# Revit family: KingswayGroup_Mrrrs_Anti-LigatureMirror
name_source: partatom
category: Specialty Equipment
units: mm (PartAtom-declared; Revit-internal decimal feet)

## family parameters
Always vertical = Yes
Cut with Voids When Loaded = No
Part Type = Normal
Room Calculation Point = No
Round Connector Dimension = Use Diameter
Shared = No
Work Plane-Based = No

## types (1)
- KingswayGroup_Mrrrs_Anti-LigatureMirror
    AssetType = Fixed
    BIMObjectName = KingswayGroup_Mirrors_Anti-LigatureMirror
    Category = Pr_40_30_53:Mirrors
    Color = For full range of available finishes and colours, contact Kingsway Group
    Default Elevation = 0 mm  [stored 0 ft]
    Description = Anti-Ligature Mirror
    DurationUnit = year
    Features = Shatter-resistant for improved safety, the KG231 Anti-Ligature Mirror is manufactured from high-strength materials to ensure durable performance. It features an impact-resistant and shatter-resistant polycarbonate mirror piece housed within an anti-ligature aluminium frame.
    Finish = For full range of available finishes and colours, contact Kingsway Group
    Manufacturer = Kingsway Group
    ManufacturerName = Kingsway Group
    ManufacturerURL = https://kingswaygroupglobal.com
    Material = Aluminium, Glass
    MirrorMaterial = NBS_Concept
    Model = KG231
    ModelNumber = KG231
    ModelReference = Anti-Ligature Mirror
    Name = Mirrors_Anti-LigatureMirror_KG231_KingswayGroup
    NominalHeight = 915 mm  [stored 3.00197 ft]
    NominalLength = 460 mm  [stored 1.50919 ft]
    NominalWidth = 13 mm
    PlateMaterial = NBS_Concept
    ProductInformation = https://kingswaygroupglobal.com
    Size = 460 x 915 x 13 mm
    URL = https://kingswaygroupglobal.com
    Uniclass2015Code = Pr_40_30_53
    Uniclass2015Title = Mirrors
    Uniclass2015Version = Products v1.36
    Version = 1
    WarrantyDescription = 5-Year Guarantee *For faulty manufacture and not for damage
    WarrantyDurationParts = 5
    WarrantyDurationUnit = year

note: [stored X ft] marks values corroborated as IEEE doubles in the binary element streams (Revit-internal decimal feet)

## geometry (parser evidence)
native form markers: Sweep x3
no freeform markers — native parametric forms only
